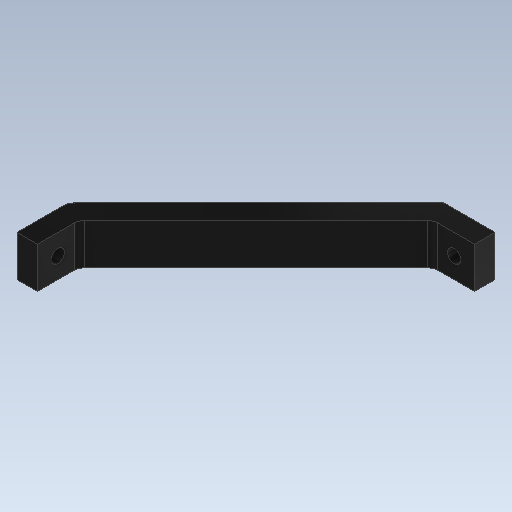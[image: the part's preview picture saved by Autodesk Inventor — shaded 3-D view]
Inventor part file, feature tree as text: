
AUTODESK INVENTOR PART (.ipt)
format: ipt  version: 2020 (Build 240168000, 168)  size: 121,344 bytes
history: native  units: mm
features: sketch x3, hole x2, extrude x1, fillet x1
ambient origin geometry x8: Origin, YZ Plane, XZ Plane, XY Plane, X Axis, Y Axis, Z Axis, Center Point
bodies: Solid1 (feature_tree)
feature tree (7):
  extrude  "Extrusion1"  Depth=25.0mm
  sketch  "Sketch2"  dims[d4=45.0deg d5=130.0mm]
  sketch  "Sketch3"  dims[d6=10.0mm d7=10.0mm d9=20.0mm d10=0.0mm d11=6.5mm d12=6.0mm d13=4.0mm d14=2.0mm d15=90.0deg d16=8.0mm d17=20.594885mm d18=6.5mm d19=6.0mm d20=4.0mm d21=2.0mm d22=90.0deg d23=8.0mm d24=20.594885mm d25=5.0mm d26=96.923882mm d27=25.0mm]
  hole  "Hole1"  [1 undecoded]
  hole  "Hole2"  [1 undecoded]
  fillet  "Fillet1"  Radius=20.0mm
  sketch  "Sketch1"  dims[d0=90.0deg d1=25.0mm]
note: 2 required parameter values undecoded (feature->parameter linkage not recoverable at this tier; creation-order binding heuristic only, values carry confidence <= 0.55)
